# Revit family: Sanitary-Hand-Dryers-Sloan-Valve-EHD-420_
name_source: partatom
category: Specialty Equipment
units: mm (PartAtom-declared; Revit-internal decimal feet)

## family parameters
Cut with Voids When Loaded = No
Host = Face
Maintain Annotation Orientation = No
OmniClass Number = 23.40.20.21.14
OmniClass Title = Hand and Hair Dryers
Part Type = Normal
Room Calculation Point = No
Round Connector Dimension = Use Diameter
Shared = No

## types (1)
- Not a Type - Load Type Catalog!
    Apparent Load = 2200 VA
    Assembly Code = C1030200
    CW Connection = Yes
    Connector Description = Electrical Connection
    Current = 20 A
    Date Updated = 09.12.2024
    Default Elevation = 0"
    Depth = 6 1/2"
    Description = Optima® Sensor-Operated Deck Hand Dryer EHD-420, HEPA110/120V
    Edition number = 1
    HW Connection = Yes
    Height = 5 1/2"
    Keynote = 15410
    Manufacturer = Sloan Valve
    Model = Model not specified - Load type catalog!
    Number of Poles = 1
    Part Number = 33660012
    Power Factor = 1
    Product Material = Sloan Valve - Finish - Polished Chrome
    Product data url = https://bimobject.com
    URL = www.sloanvalve.com
    Vent Connection = No
    Version = 2
    Voltage = 110 V
    Waste Connection = No
    Width = 1 1/2"

## geometry (parser evidence)
native form markers: Sweep x4
no freeform markers — native parametric forms only
